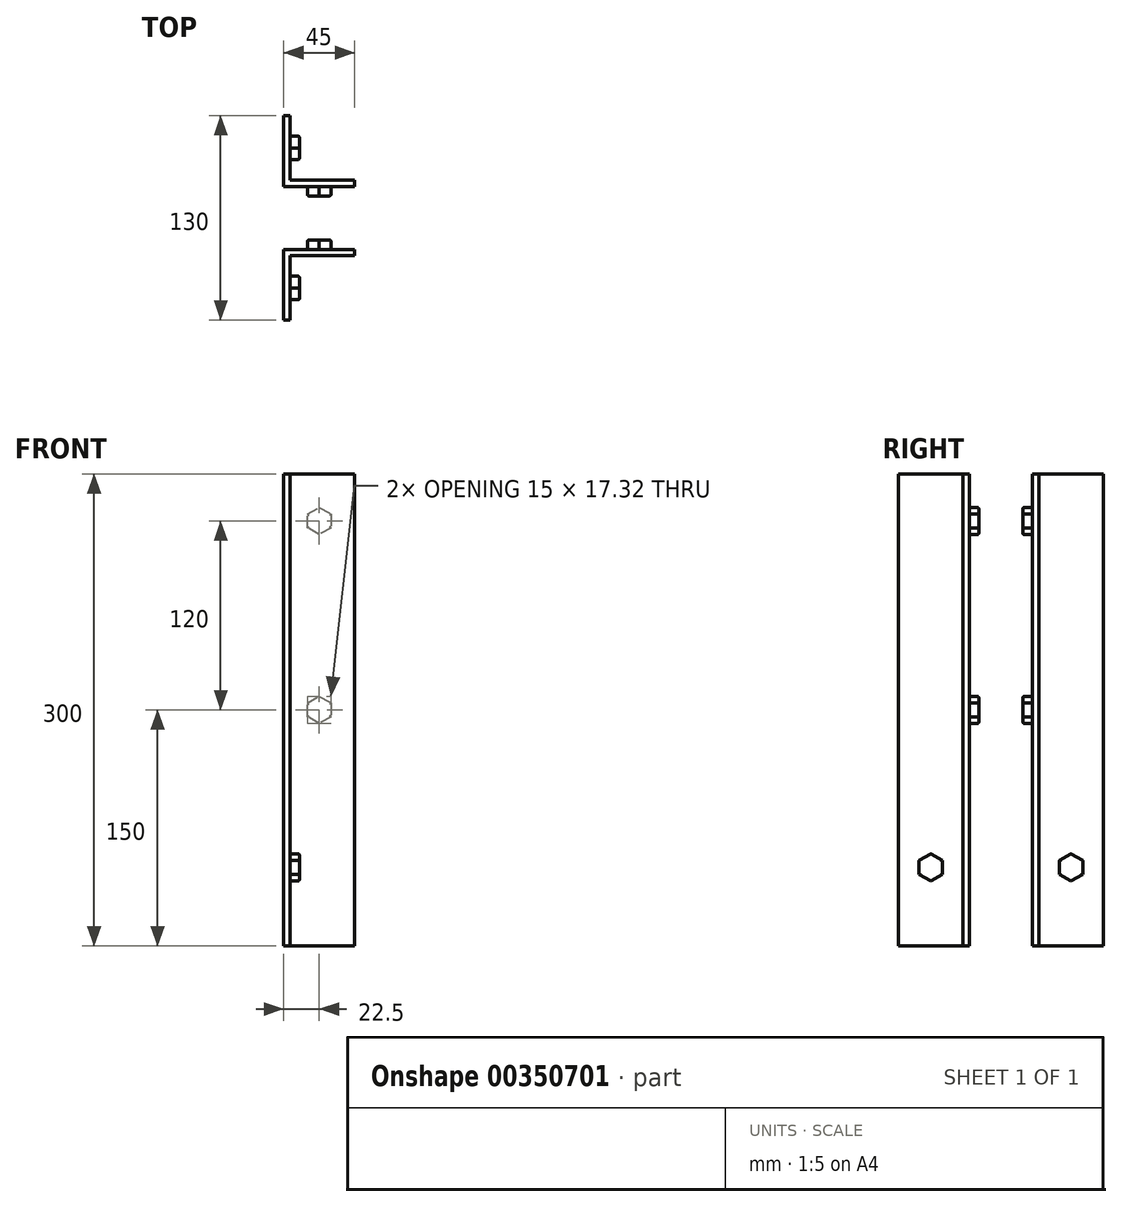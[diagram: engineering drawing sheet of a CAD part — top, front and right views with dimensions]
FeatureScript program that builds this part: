
annotation { "Feature Type Name" : "Feature", "Feature Type Description" : "" }
export const myFeature = defineFeature(function(context is Context, id is Id, definition is map)
    precondition{}
    {
        {
            var Q0;
            Q0=qCreatedBy(makeId("Top.planeOp"),FACE);
            var sketch = newSketch(context, id + "F0", { "sketchPlane" : qUnion([Q0])});
            skLineSegment(sketch, "E0", {"start": v(-10, 20) * mm, "end": v(-10, 65) * mm});
            skLineSegment(sketch, "E1", {"start": v(-10, 65) * mm, "end": v(-6, 65) * mm});
            skLineSegment(sketch, "E2", {"start": v(-6, 65) * mm, "end": v(-6, 24) * mm});
            skLineSegment(sketch, "E3", {"start": v(-10, 20) * mm, "end": v(35, 20) * mm});
            skLineSegment(sketch, "E4", {"start": v(35, 20) * mm, "end": v(35, 24) * mm});
            skLineSegment(sketch, "E5", {"start": v(35, 24) * mm, "end": v(-6, 24) * mm});
            skSolve(sketch);
        }
        {
            var Q0;
            Q0 = qSketchRegion(id + "F0", true);
            extrude(context, id + "F1", {"entities" : qUnion([Q0]), "depth" : 300 * mm});
        }
        {
            var Q0;
            Q0=makeQuery(id+"F1.opExtrude","SWEPT_FACE",FACE,{"disambiguationData":[OSD([sQuery(id+"F0.wireOp",EDGE,"E3")])]});
            var sketch = newSketch(context, id + "F2", { "sketchPlane" : qUnion([Q0])});
            skCircle(sketch, "E6.cCircle", {"center": v(12.5, 270) * mm, "radius": 7.5 * mm, "construction": true});
            skLineSegment(sketch, "E6.0", {"start": v(20, 265.67) * mm, "end": v(12.5, 261.34) * mm});
            skLineSegment(sketch, "E6.1", {"start": v(12.5, 261.34) * mm, "end": v(5, 265.67) * mm});
            skLineSegment(sketch, "E6.2", {"start": v(5, 265.67) * mm, "end": v(5, 274.33) * mm});
            skLineSegment(sketch, "E6.3", {"start": v(5, 274.33) * mm, "end": v(12.5, 278.66) * mm});
            skLineSegment(sketch, "E6.4", {"start": v(12.5, 278.66) * mm, "end": v(20, 274.33) * mm});
            skLineSegment(sketch, "E6.5", {"start": v(20, 274.33) * mm, "end": v(20, 265.67) * mm});
            skPoint(sketch, "E6.0.midPoint", {"position": v(16.25, 263.5) * mm});
            skPoint(sketch, "E7", {"position": v(12.5, 300) * mm});
            skCircle(sketch, "E8.cCircle", {"center": v(12.5, 150) * mm, "radius": 7.5 * mm, "construction": true});
            skLineSegment(sketch, "E8.0", {"start": v(20, 145.67) * mm, "end": v(12.5, 141.34) * mm});
            skLineSegment(sketch, "E8.1", {"start": v(12.5, 141.34) * mm, "end": v(5, 145.67) * mm});
            skLineSegment(sketch, "E8.2", {"start": v(5, 145.67) * mm, "end": v(5, 154.33) * mm});
            skLineSegment(sketch, "E8.3", {"start": v(5, 154.33) * mm, "end": v(12.5, 158.66) * mm});
            skLineSegment(sketch, "E8.4", {"start": v(12.5, 158.66) * mm, "end": v(20, 154.33) * mm});
            skLineSegment(sketch, "E8.5", {"start": v(20, 154.33) * mm, "end": v(20, 145.67) * mm});
            skPoint(sketch, "E8.0.midPoint", {"position": v(16.25, 143.5) * mm});
            skSolve(sketch);
        }
        {
            var Q0;
            Q0 = qSketchRegion(id + "F2", true);
            extrude(context, id + "F3", {"entities" : qUnion([Q0]), "operationType" : NewBodyOperationType.ADD, "depth" : 6 * mm});
        }
        {
            var Q0;
            Q0=makeQuery(id+"F3.opExtrude","CAP_FACE",FACE,{"disambiguationData":[OSD([sQuery(id+"F2.wireOp",EDGE,"E6.0"),sQuery(id+"F2.wireOp",EDGE,"E6.1"),sQuery(id+"F2.wireOp",EDGE,"E6.2"),sQuery(id+"F2.wireOp",EDGE,"E6.3"),sQuery(id+"F2.wireOp",EDGE,"E6.4"),sQuery(id+"F2.wireOp",EDGE,"E6.5")])],"isStart":false});
            var Q1;
            Q1=makeQuery(id+"F3.opExtrude","CAP_FACE",FACE,{"disambiguationData":[OSD([sQuery(id+"F2.wireOp",EDGE,"E8.0"),sQuery(id+"F2.wireOp",EDGE,"E8.1"),sQuery(id+"F2.wireOp",EDGE,"E8.2"),sQuery(id+"F2.wireOp",EDGE,"E8.3"),sQuery(id+"F2.wireOp",EDGE,"E8.4"),sQuery(id+"F2.wireOp",EDGE,"E8.5")])],"isStart":false});
            fillet(context, id + "F4", {"entities" : qUnion([Q0, Q1]), "radius" : 1 * mm, "tangentPropagation" : true, "allowEdgeOverflow" : false});
        }
        {
            var Q0;
            Q0=makeQuery(id+"F1.opExtrude","SWEPT_FACE",FACE,{"disambiguationData":[OSD([sQuery(id+"F0.wireOp",EDGE,"E2")])]});
            var sketch = newSketch(context, id + "F5", { "sketchPlane" : qUnion([Q0])});
            skCircle(sketch, "E9.cCircle", {"center": v(44.5, 50) * mm, "radius": 7.5 * mm, "construction": true});
            skLineSegment(sketch, "E9.0", {"start": v(52, 45.67) * mm, "end": v(44.5, 41.34) * mm});
            skLineSegment(sketch, "E9.1", {"start": v(44.5, 41.34) * mm, "end": v(37, 45.67) * mm});
            skLineSegment(sketch, "E9.2", {"start": v(37, 45.67) * mm, "end": v(37, 54.33) * mm});
            skLineSegment(sketch, "E9.3", {"start": v(37, 54.33) * mm, "end": v(44.5, 58.66) * mm});
            skLineSegment(sketch, "E9.4", {"start": v(44.5, 58.66) * mm, "end": v(52, 54.33) * mm});
            skLineSegment(sketch, "E9.5", {"start": v(52, 54.33) * mm, "end": v(52, 45.67) * mm});
            skPoint(sketch, "E9.0.midPoint", {"position": v(48.25, 43.5) * mm});
            skPoint(sketch, "E10", {"position": v(44.5, 0) * mm});
            skSolve(sketch);
        }
        {
            var Q0;
            Q0 = qSketchRegion(id + "F5", true);
            extrude(context, id + "F6", {"entities" : qUnion([Q0]), "operationType" : NewBodyOperationType.ADD, "depth" : 6 * mm});
        }
        {
            var Q0;
            Q0=makeQuery(id+"F6.opExtrude","CAP_FACE",FACE,{"disambiguationData":[OSD([sQuery(id+"F5.wireOp",EDGE,"E9.0"),sQuery(id+"F5.wireOp",EDGE,"E9.1"),sQuery(id+"F5.wireOp",EDGE,"E9.2"),sQuery(id+"F5.wireOp",EDGE,"E9.3"),sQuery(id+"F5.wireOp",EDGE,"E9.4"),sQuery(id+"F5.wireOp",EDGE,"E9.5")])],"isStart":false});
            fillet(context, id + "F7", {"entities" : qUnion([Q0]), "radius" : 1 * mm, "tangentPropagation" : true, "allowEdgeOverflow" : false});
        }
        {
            var Q0;
            Q0=makeQuery(id+"F1.opExtrude","SWEPT_BODY",BODY,{"disambiguationData":[OSD([sQuery(id+"F0.wireOp",EDGE,"E0"),sQuery(id+"F0.wireOp",EDGE,"E1"),sQuery(id+"F0.wireOp",EDGE,"E2"),sQuery(id+"F0.wireOp",EDGE,"E3"),sQuery(id+"F0.wireOp",EDGE,"E4"),sQuery(id+"F0.wireOp",EDGE,"E5")])]});
            var Q1;
            Q1=qCreatedBy(makeId("Front.planeOp"),FACE);
            mirror(context, id + "F8", {"entities" : qUnion([Q0]), "mirrorPlane" : qUnion([Q1])});
        }
    });
